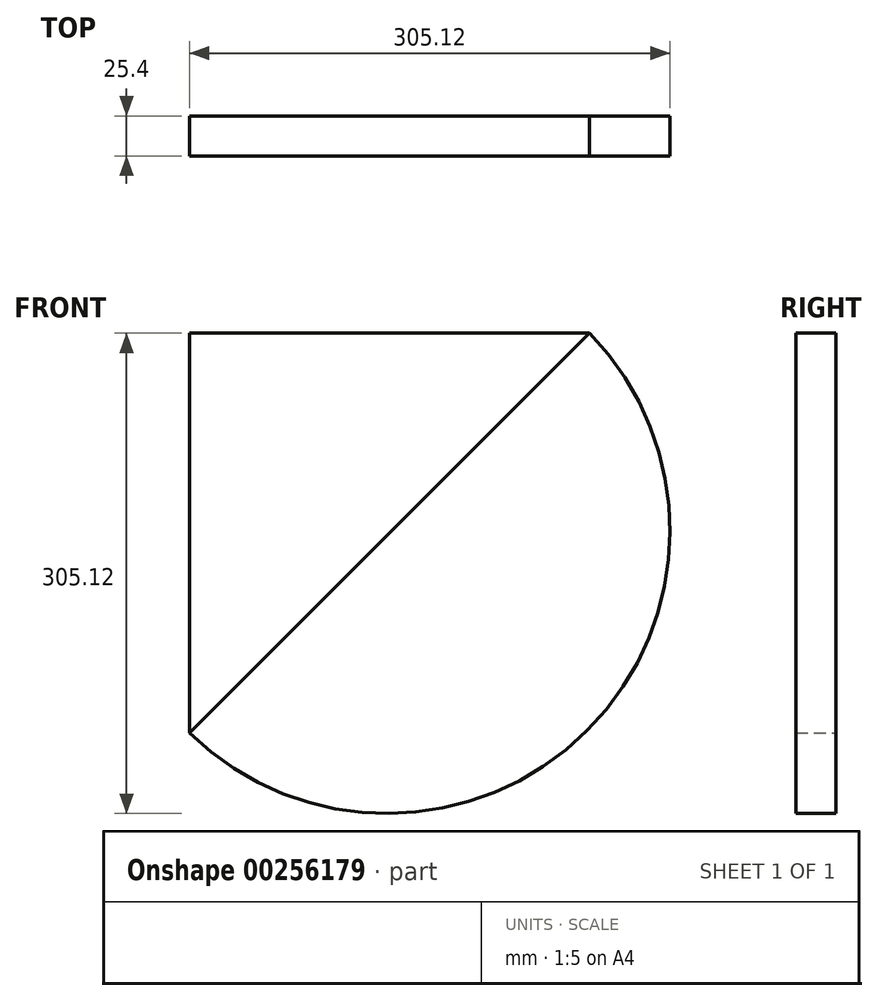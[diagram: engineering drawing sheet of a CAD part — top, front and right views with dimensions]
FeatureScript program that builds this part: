
annotation { "Feature Type Name" : "Feature", "Feature Type Description" : "" }
export const myFeature = defineFeature(function(context is Context, id is Id, definition is map)
    precondition{}
    {
        {
            var Q0;
            Q0=qCreatedBy(makeId("Front.planeOp"),FACE);
            var sketch = newSketch(context, id + "F0", { "sketchPlane" : qUnion([Q0])});
            skLineSegment(sketch, "E0.bottom", {"start": v(-127, 127) * mm, "end": v(127, 127) * mm});
            skLineSegment(sketch, "E0.left", {"start": v(-127, 127) * mm, "end": v(-127, -127) * mm});
            skPoint(sketch, "E0.middle", {"position": v(0, 0) * mm});
            skLineSegment(sketch, "E1", {"start": v(-127, -127) * mm, "end": v(127, 127) * mm});
            skPoint(sketch, "E0.right.end.orphan", {"position": v(127, -127) * mm});
            skArc(sketch, "E2", {"start": v(-127, -127) * mm, "mid": v(125.5, -125.5) * mm, "end": v(127, 127) * mm});
            skSolve(sketch);
        }
        {
            var Q0;
            Q0=makeQuery(id+"F0.imprint","IMPRINT",FACE,{"disambiguationData":[TD([[makeQuery(id+"F0.imprint","IMPRINT",EDGE,{"derivedFrom":sQuery(id+"F0.wireOp",EDGE,"E0.bottom")}),-1.0]])]});
            extrude(context, id + "F1", {"entities" : qUnion([Q0]), "depth" : 25.4 * mm});
        }
        {
            var Q0;
            Q0=makeQuery(id+"F0.imprint","IMPRINT",FACE,{"disambiguationData":[TD([[makeQuery(id+"F0.imprint","IMPRINT",EDGE,{"derivedFrom":sQuery(id+"F0.wireOp",EDGE,"E1")}),-1.0]])]});
            extrude(context, id + "F2", {"entities" : qUnion([Q0]), "depth" : 25.4 * mm});
        }
    });
